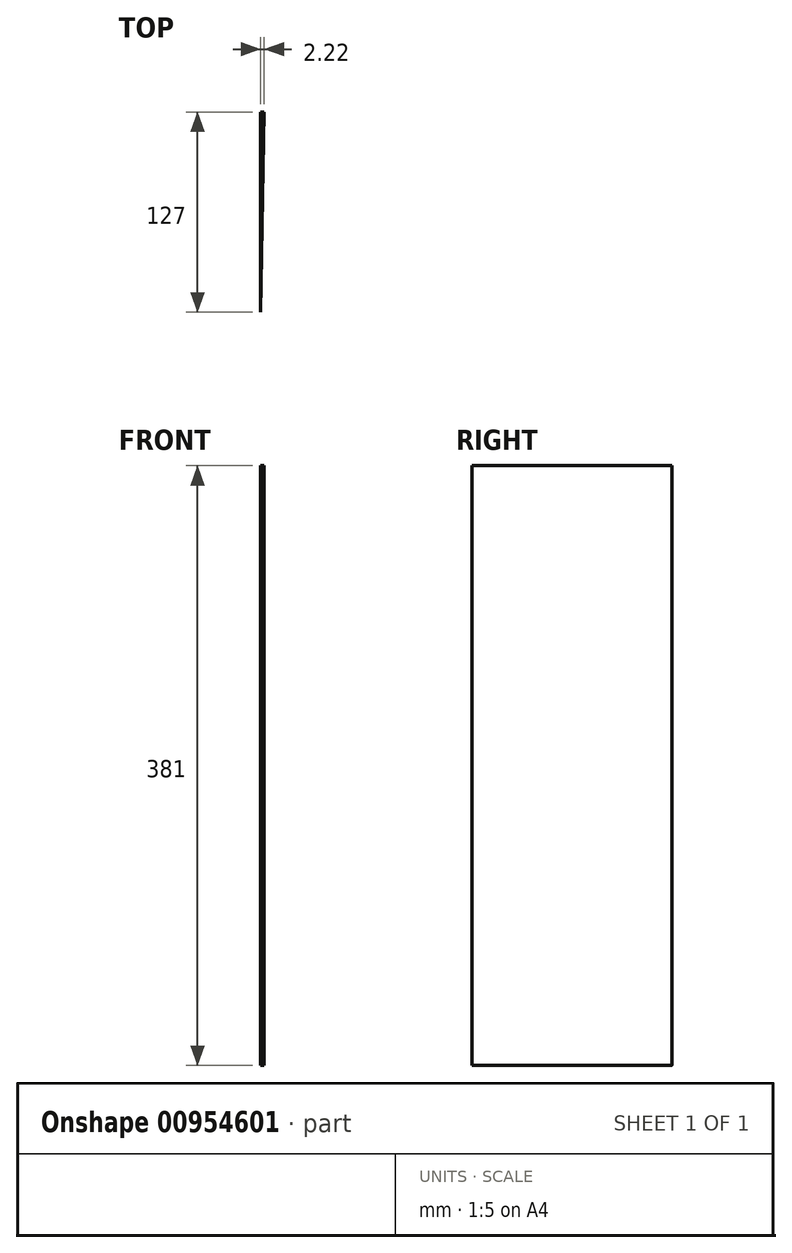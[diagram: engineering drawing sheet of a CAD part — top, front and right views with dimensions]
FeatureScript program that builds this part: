
annotation { "Feature Type Name" : "Feature", "Feature Type Description" : "" }
export const myFeature = defineFeature(function(context is Context, id is Id, definition is map)
    precondition{}
    {
        {
            var Q0;
            Q0=qCreatedBy(makeId("Top.planeOp"),FACE);
            var sketch = newSketch(context, id + "F0", { "sketchPlane" : qUnion([Q0])});
            skArc(sketch, "E0", {"start": v(2.22, 126.98) * mm, "mid": v(1.1, 127) * mm, "end": v(0, 127) * mm});
            skLineSegment(sketch, "E1", {"start": v(0, 0) * mm, "end": v(0, 127) * mm});
            skLineSegment(sketch, "E2", {"start": v(2.22, 126.98) * mm, "end": v(0, 0) * mm});
            skSolve(sketch);
        }
        {
            var Q0;
            Q0 = qSketchRegion(id + "F0", true);
            extrude(context, id + "F1", {"entities" : qUnion([Q0]), "depth" : 381 * mm, "offsetDistance" : 25.4 * mm});
        }
    });
